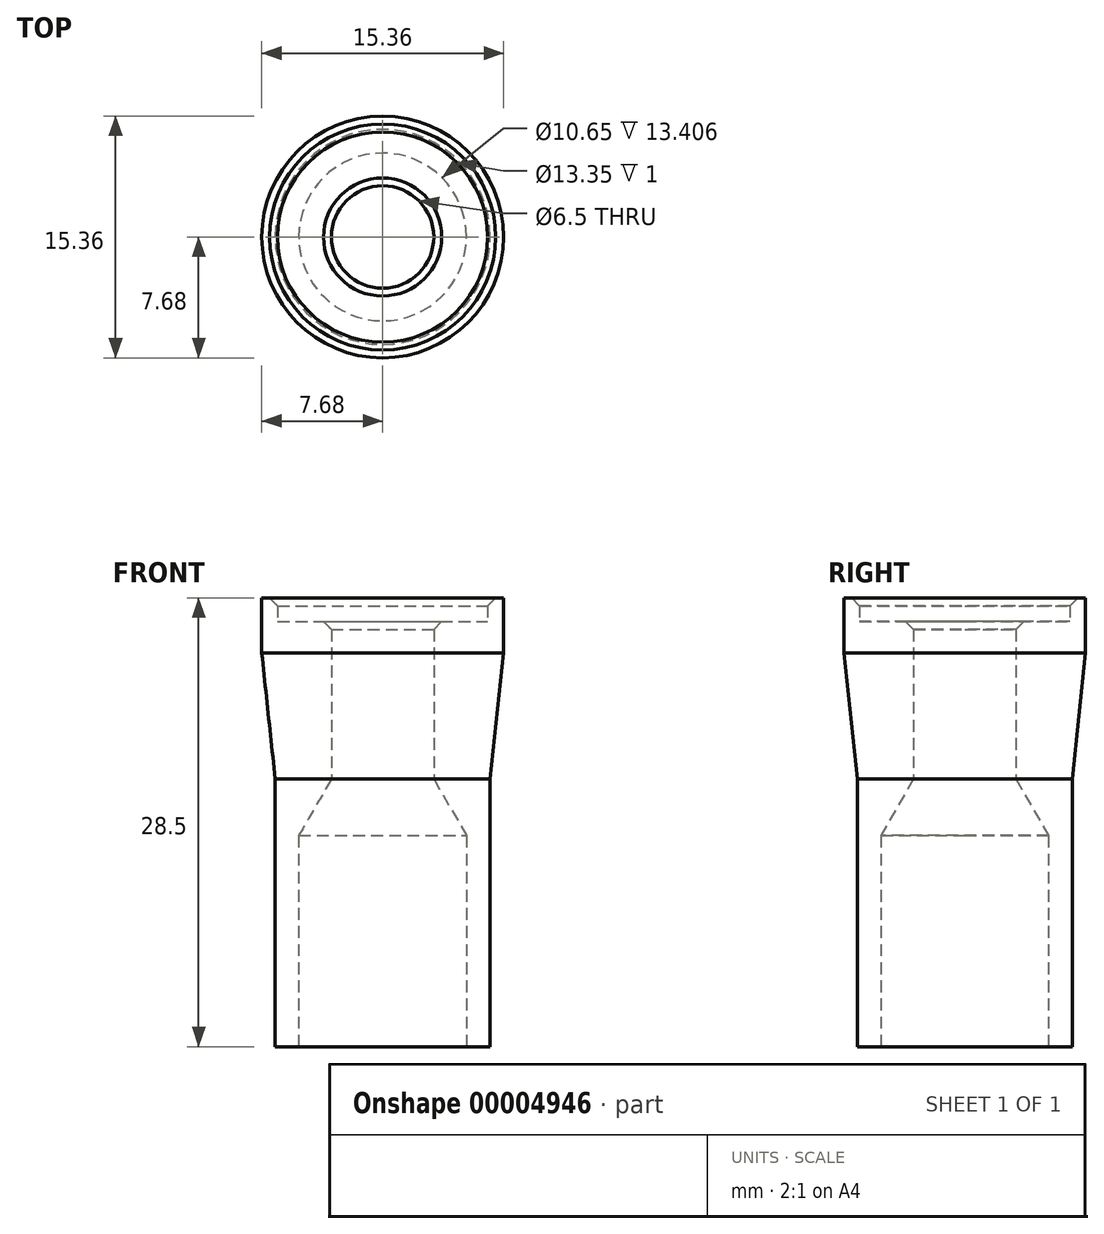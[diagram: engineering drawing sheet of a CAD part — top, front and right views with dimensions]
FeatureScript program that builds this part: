
annotation { "Feature Type Name" : "Feature", "Feature Type Description" : "" }
export const myFeature = defineFeature(function(context is Context, id is Id, definition is map)
    precondition{}
    {
        {
            var Q0;
            Q0=qCreatedBy(makeId("Front.planeOp"),FACE);
            var sketch = newSketch(context, id + "F0", { "sketchPlane" : qUnion([Q0])});
            skLineSegment(sketch, "E0", {"start": v(0, 0) * mm, "end": v(0, 28.5) * mm, "construction": true});
            skLineSegment(sketch, "E1", {"start": v(5.33, 0) * mm, "end": v(5.33, 13.4) * mm});
            skLineSegment(sketch, "E2", {"start": v(6.67, 28.5) * mm, "end": v(7.67, 28.5) * mm});
            skLineSegment(sketch, "E3", {"start": v(7.67, 28.5) * mm, "end": v(7.67, 25) * mm});
            skLineSegment(sketch, "E4", {"start": v(6.83, 0) * mm, "end": v(5.33, 0) * mm});
            skLineSegment(sketch, "E5", {"start": v(5.33, 13.4) * mm, "end": v(3.25, 17) * mm});
            skLineSegment(sketch, "E6", {"start": v(3.25, 17) * mm, "end": v(3.25, 27) * mm});
            skLineSegment(sketch, "E7", {"start": v(3.25, 27) * mm, "end": v(6.67, 27) * mm});
            skLineSegment(sketch, "E8", {"start": v(6.67, 28.5) * mm, "end": v(6.67, 27) * mm});
            skLineSegment(sketch, "E9", {"start": v(6.83, 0) * mm, "end": v(6.83, 17) * mm});
            skLineSegment(sketch, "E10", {"start": v(6.83, 17) * mm, "end": v(7.67, 25) * mm});
            skLineSegment(sketch, "E11", {"start": v(7.67, 25) * mm, "end": v(7.68, 0) * mm, "construction": true});
            skLineSegment(sketch, "E12", {"start": v(7.68, 0) * mm, "end": v(6.83, 0) * mm, "construction": true});
            skLineSegment(sketch, "E13", {"start": v(0, 28.5) * mm, "end": v(6.67, 28.5) * mm, "construction": true});
            skSolve(sketch);
        }
        {
            var Q0;
            Q0 = qSketchRegion(id + "F0", true);
            var Q1;
            Q1=sQuery(id+"F0.wireOp",EDGE,"E0");
            revolve(context, id + "F1", {"entities" : qUnion([Q0]), "axis" : qUnion([Q1]), "revolveType" : RevolveType.FULL});
        }
        {
            var Q0;
            Q0=makeQuery(id+"F1.opRevolve","SWEPT_EDGE",EDGE,{"disambiguationData":[OSD([sQuery(id+"F0.wireOp",EDGE,"E2"),sQuery(id+"F0.wireOp",EDGE,"E8")])]});
            var Q1;
            Q1=makeQuery(id+"F1.opRevolve","SWEPT_EDGE",EDGE,{"disambiguationData":[OSD([sQuery(id+"F0.wireOp",EDGE,"E6"),sQuery(id+"F0.wireOp",EDGE,"E7")])]});
            chamfer(context, id + "F2", {"entities" : qUnion([Q0, Q1]), "width" : 0.5 * mm, "tangentPropagation" : true});
        }
    });
